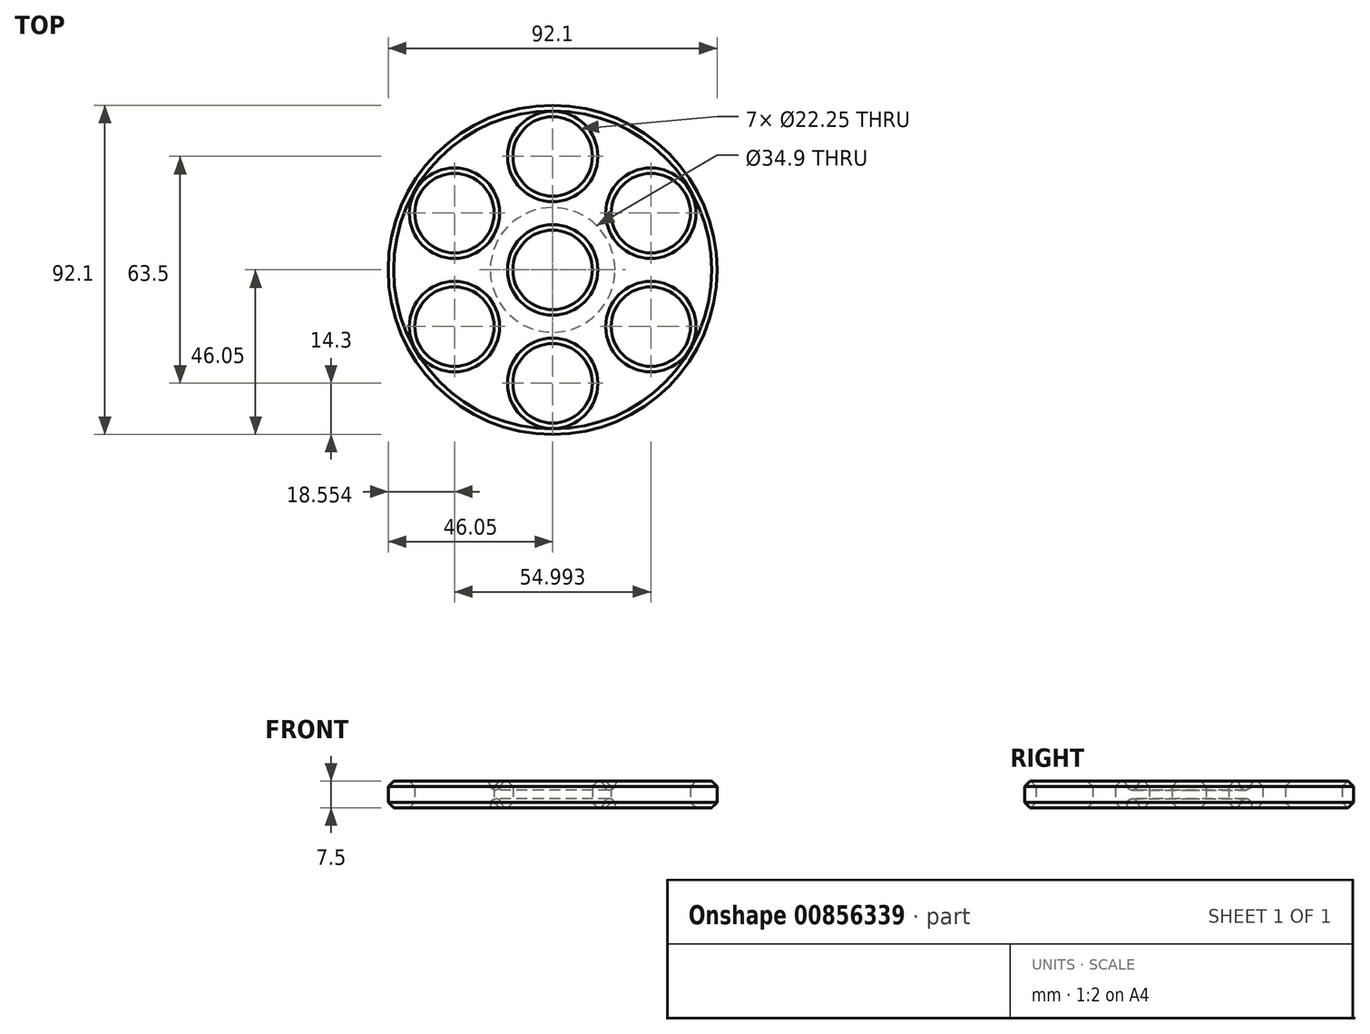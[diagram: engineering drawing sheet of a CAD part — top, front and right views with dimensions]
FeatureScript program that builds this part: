
annotation { "Feature Type Name" : "Feature", "Feature Type Description" : "" }
export const myFeature = defineFeature(function(context is Context, id is Id, definition is map)
    precondition{}
    {
        {
            var Q0;
            Q0=qCreatedBy(makeId("Top.planeOp"),FACE);
            var sketch = newSketch(context, id + "F0", { "sketchPlane" : qUnion([Q0])});
            skCircle(sketch, "E0", {"center": v(0, 0) * mm, "radius": 11.12 * mm});
            skCircle(sketch, "E1", {"center": v(0, 31.75) * mm, "radius": 11.12 * mm});
            skCircle(sketch, "E2", {"center": v(0, -31.75) * mm, "radius": 11.12 * mm});
            skCircle(sketch, "E3", {"center": v(0, 31.75) * mm, "radius": 14.3 * mm});
            skCircle(sketch, "E4", {"center": v(0, 0) * mm, "radius": 14.3 * mm});
            skCircle(sketch, "E5", {"center": v(0, -31.75) * mm, "radius": 14.3 * mm});
            skCircle(sketch, "E6", {"center": v(0, 0) * mm, "radius": 42.88 * mm});
            skCircle(sketch, "E7", {"center": v(0, 0) * mm, "radius": 46.05 * mm});
            skCircle(sketch, "E8.1.0", {"center": v(27.5, 15.87) * mm, "radius": 14.3 * mm});
            skCircle(sketch, "E8.1.1", {"center": v(27.5, 15.87) * mm, "radius": 11.12 * mm});
            skCircle(sketch, "E8.1.2", {"center": v(-27.5, -15.87) * mm, "radius": 11.12 * mm});
            skCircle(sketch, "E8.1.3", {"center": v(-27.5, -15.87) * mm, "radius": 14.3 * mm});
            skCircle(sketch, "E8.2.0", {"center": v(-27.5, 15.88) * mm, "radius": 14.3 * mm});
            skCircle(sketch, "E8.2.1", {"center": v(-27.5, 15.88) * mm, "radius": 11.12 * mm});
            skCircle(sketch, "E8.2.2", {"center": v(27.5, -15.88) * mm, "radius": 11.12 * mm});
            skCircle(sketch, "E8.2.3", {"center": v(27.5, -15.88) * mm, "radius": 14.3 * mm});
            skCircle(sketch, "E9", {"center": v(0, 0) * mm, "radius": 20.62 * mm});
            skCircle(sketch, "E10", {"center": v(0, 0) * mm, "radius": 17.45 * mm});
            skSolve(sketch);
        }
        {
            var Q0;
            Q0 = qSketchRegion(id + "F0", true);
            var Q1;
            {var subQ0=sQuery(id+"F0.wireOp",EDGE,"E6");var subQ1=sQuery(id+"F0.wireOp",EDGE,"E1");var subQ2=makeQuery(id+"F0.imprint","INTERSECT",VERTEX,{"derivedFrom":[subQ1,subQ0]});Q1=makeQuery(id+"F0.imprint","IMPRINT",FACE,{"disambiguationData":[TD([[makeQuery(id+"F0.imprint","IMPRINT",EDGE,{"disambiguationData":[TD([[subQ2,1.0]])],"derivedFrom":subQ1}),-1.0]])]});}
            var Q2;
            {var subQ0=sQuery(id+"F0.wireOp",EDGE,"E6");var subQ1=sQuery(id+"F0.wireOp",EDGE,"E1");var subQ2=makeQuery(id+"F0.imprint","INTERSECT",VERTEX,{"derivedFrom":[subQ1,subQ0]});Q2=makeQuery(id+"F0.imprint","IMPRINT",FACE,{"disambiguationData":[TD([[makeQuery(id+"F0.imprint","IMPRINT",EDGE,{"disambiguationData":[TD([[subQ2,-1.0]])],"derivedFrom":subQ1}),-1.0]])]});}
            var Q3;
            {var subQ0=sQuery(id+"F0.wireOp",EDGE,"E9");var subQ1=sQuery(id+"F0.wireOp",EDGE,"E3");var subQ2=makeQuery(id+"F0.imprint","INTERSECT",VERTEX,{"disambiguationData":[OD(0.0)],"derivedFrom":[subQ1,subQ0]});Q3=makeQuery(id+"F0.imprint","IMPRINT",FACE,{"disambiguationData":[TD([[makeQuery(id+"F0.imprint","IMPRINT",EDGE,{"disambiguationData":[TD([[subQ2,-1.0]])],"derivedFrom":subQ1}),1.0]])]});}
            var Q4;
            {var subQ0=sQuery(id+"F0.wireOp",EDGE,"E8.1.0");var subQ1=makeQuery(id+"F0.imprint","INTERSECT",VERTEX,{"derivedFrom":[subQ0,sQuery(id+"F0.wireOp",EDGE,"E10")]});Q4=makeQuery(id+"F0.imprint","IMPRINT",FACE,{"disambiguationData":[TD([[makeQuery(id+"F0.imprint","IMPRINT",EDGE,{"disambiguationData":[TD([[subQ1,1.0]])],"derivedFrom":subQ0}),1.0]])]});}
            var Q5;
            {var subQ0=sQuery(id+"F0.wireOp",EDGE,"E10");var subQ1=sQuery(id+"F0.wireOp",EDGE,"E3");var subQ2=makeQuery(id+"F0.imprint","INTERSECT",VERTEX,{"derivedFrom":[subQ1,subQ0]});Q5=makeQuery(id+"F0.imprint","IMPRINT",FACE,{"disambiguationData":[TD([[makeQuery(id+"F0.imprint","IMPRINT",EDGE,{"disambiguationData":[TD([[subQ2,-1.0]])],"derivedFrom":subQ1}),-1.0]])]});}
            var Q6;
            {var subQ0=sQuery(id+"F0.wireOp",EDGE,"E10");var subQ1=sQuery(id+"F0.wireOp",EDGE,"E8.1.0");var subQ2=makeQuery(id+"F0.imprint","INTERSECT",VERTEX,{"derivedFrom":[subQ1,subQ0]});Q6=makeQuery(id+"F0.imprint","IMPRINT",FACE,{"disambiguationData":[TD([[makeQuery(id+"F0.imprint","IMPRINT",EDGE,{"disambiguationData":[TD([[subQ2,-1.0]])],"derivedFrom":subQ1}),-1.0]])]});}
            var Q7;
            {var subQ0=sQuery(id+"F0.wireOp",EDGE,"E9");var subQ1=sQuery(id+"F0.wireOp",EDGE,"E8.2.3");var subQ2=makeQuery(id+"F0.imprint","INTERSECT",VERTEX,{"disambiguationData":[OD(0.0)],"derivedFrom":[subQ1,subQ0]});Q7=makeQuery(id+"F0.imprint","IMPRINT",FACE,{"disambiguationData":[TD([[makeQuery(id+"F0.imprint","IMPRINT",EDGE,{"disambiguationData":[TD([[subQ2,-1.0]])],"derivedFrom":subQ1}),1.0]])]});}
            var Q8;
            {var subQ0=sQuery(id+"F0.wireOp",EDGE,"E10");var subQ1=sQuery(id+"F0.wireOp",EDGE,"E5");var subQ2=makeQuery(id+"F0.imprint","INTERSECT",VERTEX,{"derivedFrom":[subQ1,subQ0]});Q8=makeQuery(id+"F0.imprint","IMPRINT",FACE,{"disambiguationData":[TD([[makeQuery(id+"F0.imprint","IMPRINT",EDGE,{"disambiguationData":[TD([[subQ2,1.0]])],"derivedFrom":subQ1}),-1.0]])]});}
            var Q9;
            {var subQ0=sQuery(id+"F0.wireOp",EDGE,"E5");var subQ1=makeQuery(id+"F0.imprint","INTERSECT",VERTEX,{"derivedFrom":[subQ0,sQuery(id+"F0.wireOp",EDGE,"E10")]});Q9=makeQuery(id+"F0.imprint","IMPRINT",FACE,{"disambiguationData":[TD([[makeQuery(id+"F0.imprint","IMPRINT",EDGE,{"disambiguationData":[TD([[subQ1,1.0]])],"derivedFrom":subQ0}),1.0]])]});}
            var Q10;
            {var subQ0=sQuery(id+"F0.wireOp",EDGE,"E10");var subQ1=sQuery(id+"F0.wireOp",EDGE,"E5");var subQ2=makeQuery(id+"F0.imprint","INTERSECT",VERTEX,{"derivedFrom":[subQ1,subQ0]});Q10=makeQuery(id+"F0.imprint","IMPRINT",FACE,{"disambiguationData":[TD([[makeQuery(id+"F0.imprint","IMPRINT",EDGE,{"disambiguationData":[TD([[subQ2,-1.0]])],"derivedFrom":subQ1}),-1.0]])]});}
            var Q11;
            {var subQ0=sQuery(id+"F0.wireOp",EDGE,"E9");var subQ1=sQuery(id+"F0.wireOp",EDGE,"E8.1.3");var subQ2=makeQuery(id+"F0.imprint","INTERSECT",VERTEX,{"disambiguationData":[OD(0.0)],"derivedFrom":[subQ1,subQ0]});Q11=makeQuery(id+"F0.imprint","IMPRINT",FACE,{"disambiguationData":[TD([[makeQuery(id+"F0.imprint","IMPRINT",EDGE,{"disambiguationData":[TD([[subQ2,-1.0]])],"derivedFrom":subQ1}),1.0]])]});}
            var Q12;
            {var subQ0=sQuery(id+"F0.wireOp",EDGE,"E10");var subQ1=sQuery(id+"F0.wireOp",EDGE,"E8.1.3");var subQ2=makeQuery(id+"F0.imprint","INTERSECT",VERTEX,{"derivedFrom":[subQ1,subQ0]});Q12=makeQuery(id+"F0.imprint","IMPRINT",FACE,{"disambiguationData":[TD([[makeQuery(id+"F0.imprint","IMPRINT",EDGE,{"disambiguationData":[TD([[subQ2,-1.0]])],"derivedFrom":subQ1}),-1.0]])]});}
            var Q13;
            {var subQ0=sQuery(id+"F0.wireOp",EDGE,"E8.2.0");var subQ1=makeQuery(id+"F0.imprint","INTERSECT",VERTEX,{"derivedFrom":[subQ0,sQuery(id+"F0.wireOp",EDGE,"E10")]});Q13=makeQuery(id+"F0.imprint","IMPRINT",FACE,{"disambiguationData":[TD([[makeQuery(id+"F0.imprint","IMPRINT",EDGE,{"disambiguationData":[TD([[subQ1,1.0]])],"derivedFrom":subQ0}),1.0]])]});}
            var Q14;
            {var subQ0=sQuery(id+"F0.wireOp",EDGE,"E9");var subQ1=sQuery(id+"F0.wireOp",EDGE,"E3");var subQ2=makeQuery(id+"F0.imprint","INTERSECT",VERTEX,{"disambiguationData":[OD(0.0)],"derivedFrom":[subQ1,subQ0]});Q14=makeQuery(id+"F0.imprint","IMPRINT",FACE,{"disambiguationData":[TD([[makeQuery(id+"F0.imprint","IMPRINT",EDGE,{"disambiguationData":[TD([[subQ2,-1.0]])],"derivedFrom":subQ1}),-1.0]])]});}
            var Q15;
            {var subQ0=sQuery(id+"F0.wireOp",EDGE,"E8.2.0");var subQ1=sQuery(id+"F0.wireOp",EDGE,"E6");var subQ2=makeQuery(id+"F0.imprint","INTERSECT",VERTEX,{"disambiguationData":[OD(0.0)],"derivedFrom":[subQ1,subQ0]});Q15=makeQuery(id+"F0.imprint","IMPRINT",FACE,{"disambiguationData":[TD([[makeQuery(id+"F0.imprint","IMPRINT",EDGE,{"disambiguationData":[TD([[subQ2,-1.0]])],"derivedFrom":subQ1}),1.0]])]});}
            var Q16;
            {var subQ0=sQuery(id+"F0.wireOp",EDGE,"E8.2.1");var subQ1=sQuery(id+"F0.wireOp",EDGE,"E6");var subQ2=makeQuery(id+"F0.imprint","INTERSECT",VERTEX,{"derivedFrom":[subQ1,subQ0]});Q16=makeQuery(id+"F0.imprint","IMPRINT",FACE,{"disambiguationData":[TD([[makeQuery(id+"F0.imprint","IMPRINT",EDGE,{"disambiguationData":[TD([[subQ2,-1.0]])],"derivedFrom":subQ1}),1.0]])]});}
            var Q17;
            {var subQ0=sQuery(id+"F0.wireOp",EDGE,"E8.2.0");var subQ1=sQuery(id+"F0.wireOp",EDGE,"E6");var subQ2=makeQuery(id+"F0.imprint","INTERSECT",VERTEX,{"disambiguationData":[OD(1.0)],"derivedFrom":[subQ1,subQ0]});Q17=makeQuery(id+"F0.imprint","IMPRINT",FACE,{"disambiguationData":[TD([[makeQuery(id+"F0.imprint","IMPRINT",EDGE,{"disambiguationData":[TD([[subQ2,-1.0]])],"derivedFrom":subQ1}),1.0]])]});}
            var Q18;
            {var subQ0=sQuery(id+"F0.wireOp",EDGE,"E6");var subQ1=sQuery(id+"F0.wireOp",EDGE,"E3");var subQ2=makeQuery(id+"F0.imprint","INTERSECT",VERTEX,{"disambiguationData":[OD(1.0)],"derivedFrom":[subQ1,subQ0]});Q18=makeQuery(id+"F0.imprint","IMPRINT",FACE,{"disambiguationData":[TD([[makeQuery(id+"F0.imprint","IMPRINT",EDGE,{"disambiguationData":[TD([[subQ2,-1.0]])],"derivedFrom":subQ1}),-1.0]])]});}
            var Q19;
            {var subQ0=sQuery(id+"F0.wireOp",EDGE,"E6");var subQ1=sQuery(id+"F0.wireOp",EDGE,"E3");var subQ2=makeQuery(id+"F0.imprint","INTERSECT",VERTEX,{"disambiguationData":[OD(0.0)],"derivedFrom":[subQ1,subQ0]});Q19=makeQuery(id+"F0.imprint","IMPRINT",FACE,{"disambiguationData":[TD([[makeQuery(id+"F0.imprint","IMPRINT",EDGE,{"disambiguationData":[TD([[subQ2,1.0]])],"derivedFrom":subQ1}),-1.0]])]});}
            var Q20;
            {var subQ0=sQuery(id+"F0.wireOp",EDGE,"E8.1.1");var subQ1=sQuery(id+"F0.wireOp",EDGE,"E6");var subQ2=makeQuery(id+"F0.imprint","INTERSECT",VERTEX,{"derivedFrom":[subQ1,subQ0]});Q20=makeQuery(id+"F0.imprint","IMPRINT",FACE,{"disambiguationData":[TD([[makeQuery(id+"F0.imprint","IMPRINT",EDGE,{"disambiguationData":[TD([[subQ2,-1.0]])],"derivedFrom":subQ1}),1.0]])]});}
            var Q21;
            {var subQ0=sQuery(id+"F0.wireOp",EDGE,"E8.1.1");var subQ1=sQuery(id+"F0.wireOp",EDGE,"E6");var subQ2=makeQuery(id+"F0.imprint","INTERSECT",VERTEX,{"derivedFrom":[subQ1,subQ0]});Q21=makeQuery(id+"F0.imprint","IMPRINT",FACE,{"disambiguationData":[TD([[makeQuery(id+"F0.imprint","IMPRINT",EDGE,{"disambiguationData":[TD([[subQ2,1.0]])],"derivedFrom":subQ1}),1.0]])]});}
            var Q22;
            {var subQ0=sQuery(id+"F0.wireOp",EDGE,"E8.1.0");var subQ1=sQuery(id+"F0.wireOp",EDGE,"E6");var subQ2=makeQuery(id+"F0.imprint","INTERSECT",VERTEX,{"disambiguationData":[OD(0.0)],"derivedFrom":[subQ1,subQ0]});Q22=makeQuery(id+"F0.imprint","IMPRINT",FACE,{"disambiguationData":[TD([[makeQuery(id+"F0.imprint","IMPRINT",EDGE,{"disambiguationData":[TD([[subQ2,1.0]])],"derivedFrom":subQ1}),1.0]])]});}
            var Q23;
            {var subQ0=sQuery(id+"F0.wireOp",EDGE,"E8.2.2");var subQ1=sQuery(id+"F0.wireOp",EDGE,"E6");var subQ2=makeQuery(id+"F0.imprint","INTERSECT",VERTEX,{"derivedFrom":[subQ1,subQ0]});Q23=makeQuery(id+"F0.imprint","IMPRINT",FACE,{"disambiguationData":[TD([[makeQuery(id+"F0.imprint","IMPRINT",EDGE,{"disambiguationData":[TD([[subQ2,-1.0]])],"derivedFrom":subQ1}),1.0]])]});}
            var Q24;
            {var subQ0=sQuery(id+"F0.wireOp",EDGE,"E8.2.3");var subQ1=sQuery(id+"F0.wireOp",EDGE,"E6");var subQ2=makeQuery(id+"F0.imprint","INTERSECT",VERTEX,{"disambiguationData":[OD(0.0)],"derivedFrom":[subQ1,subQ0]});Q24=makeQuery(id+"F0.imprint","IMPRINT",FACE,{"disambiguationData":[TD([[makeQuery(id+"F0.imprint","IMPRINT",EDGE,{"disambiguationData":[TD([[subQ2,-1.0]])],"derivedFrom":subQ1}),1.0]])]});}
            var Q25;
            {var subQ0=sQuery(id+"F0.wireOp",EDGE,"E6");var subQ1=sQuery(id+"F0.wireOp",EDGE,"E2");var subQ2=makeQuery(id+"F0.imprint","INTERSECT",VERTEX,{"derivedFrom":[subQ1,subQ0]});Q25=makeQuery(id+"F0.imprint","IMPRINT",FACE,{"disambiguationData":[TD([[makeQuery(id+"F0.imprint","IMPRINT",EDGE,{"disambiguationData":[TD([[subQ2,1.0]])],"derivedFrom":subQ1}),-1.0]])]});}
            var Q26;
            {var subQ0=sQuery(id+"F0.wireOp",EDGE,"E9");var subQ1=sQuery(id+"F0.wireOp",EDGE,"E5");var subQ2=makeQuery(id+"F0.imprint","INTERSECT",VERTEX,{"disambiguationData":[OD(1.0)],"derivedFrom":[subQ1,subQ0]});Q26=makeQuery(id+"F0.imprint","IMPRINT",FACE,{"disambiguationData":[TD([[makeQuery(id+"F0.imprint","IMPRINT",EDGE,{"disambiguationData":[TD([[subQ2,-1.0]])],"derivedFrom":subQ1}),-1.0]])]});}
            var Q27;
            {var subQ0=sQuery(id+"F0.wireOp",EDGE,"E9");var subQ1=sQuery(id+"F0.wireOp",EDGE,"E5");var subQ2=makeQuery(id+"F0.imprint","INTERSECT",VERTEX,{"disambiguationData":[OD(0.0)],"derivedFrom":[subQ1,subQ0]});Q27=makeQuery(id+"F0.imprint","IMPRINT",FACE,{"disambiguationData":[TD([[makeQuery(id+"F0.imprint","IMPRINT",EDGE,{"disambiguationData":[TD([[subQ2,1.0]])],"derivedFrom":subQ1}),-1.0]])]});}
            var Q28;
            {var subQ0=sQuery(id+"F0.wireOp",EDGE,"E6");var subQ1=sQuery(id+"F0.wireOp",EDGE,"E2");var subQ2=makeQuery(id+"F0.imprint","INTERSECT",VERTEX,{"derivedFrom":[subQ1,subQ0]});Q28=makeQuery(id+"F0.imprint","IMPRINT",FACE,{"disambiguationData":[TD([[makeQuery(id+"F0.imprint","IMPRINT",EDGE,{"disambiguationData":[TD([[subQ2,-1.0]])],"derivedFrom":subQ1}),-1.0]])]});}
            var Q29;
            {var subQ0=sQuery(id+"F0.wireOp",EDGE,"E8.1.2");var subQ1=sQuery(id+"F0.wireOp",EDGE,"E6");var subQ2=makeQuery(id+"F0.imprint","INTERSECT",VERTEX,{"derivedFrom":[subQ1,subQ0]});Q29=makeQuery(id+"F0.imprint","IMPRINT",FACE,{"disambiguationData":[TD([[makeQuery(id+"F0.imprint","IMPRINT",EDGE,{"disambiguationData":[TD([[subQ2,-1.0]])],"derivedFrom":subQ1}),1.0]])]});}
            var Q30;
            {var subQ0=sQuery(id+"F0.wireOp",EDGE,"E8.1.3");var subQ1=sQuery(id+"F0.wireOp",EDGE,"E6");var subQ2=makeQuery(id+"F0.imprint","INTERSECT",VERTEX,{"disambiguationData":[OD(0.0)],"derivedFrom":[subQ1,subQ0]});Q30=makeQuery(id+"F0.imprint","IMPRINT",FACE,{"disambiguationData":[TD([[makeQuery(id+"F0.imprint","IMPRINT",EDGE,{"disambiguationData":[TD([[subQ2,-1.0]])],"derivedFrom":subQ1}),1.0]])]});}
            var Q31;
            Q31=makeQuery(id+"F0.imprint","IMPRINT",FACE,{"disambiguationData":[TD([[makeQuery(id+"F0.imprint","IMPRINT",EDGE,{"derivedFrom":sQuery(id+"F0.wireOp",EDGE,"E0")}),-1.0]])]});
            var Q32;
            Q32=makeQuery(id+"F0.imprint","IMPRINT",FACE,{"disambiguationData":[TD([[makeQuery(id+"F0.imprint","IMPRINT",EDGE,{"derivedFrom":sQuery(id+"F0.wireOp",EDGE,"E4")}),-1.0]])]});
            extrude(context, id + "F1", {"entities" : qUnion([Q0, Q1, Q2, Q3, Q4, Q5, Q6, Q7, Q8, Q9, Q10, Q11, Q12, Q13, Q14, Q15, Q16, Q17, Q18, Q19, Q20, Q21, Q22, Q23, Q24, Q25, Q26, Q27, Q28, Q29, Q30, Q31, Q32]), "depth" : 7.5 * mm, "offsetDistance" : 25 * mm});
        }
        {
            var Q0;
            Q0=makeQuery(id+"F0.imprint","IMPRINT",FACE,{"disambiguationData":[TD([[makeQuery(id+"F0.imprint","IMPRINT",EDGE,{"derivedFrom":sQuery(id+"F0.wireOp",EDGE,"E4")}),-1.0]])]});
            extrude(context, id + "F2", {"entities" : qUnion([Q0]), "operationType" : NewBodyOperationType.REMOVE, "depth" : 7.5 / 3 * mm, "offsetDistance" : 25 * mm});
        }
        {
            var Q0;
            Q0=makeQuery(id+"F0.imprint","IMPRINT",FACE,{"disambiguationData":[TD([[makeQuery(id+"F0.imprint","IMPRINT",EDGE,{"derivedFrom":sQuery(id+"F0.wireOp",EDGE,"E4")}),-1.0]])]});
            extrude(context, id + "F3", {"entities" : qUnion([Q0]), "operationType" : NewBodyOperationType.REMOVE, "depth" : 25 * mm, "offsetDistance" : 25 * mm, "hasSecondDirection" : true, "secondDirectionOppositeDirection" : false, "secondDirectionDepth" : (7.5 / 3) * 2 * mm});
        }
        {
            var Q0;
            Q0=makeQuery(id+"F3.boolean.opBoolean","COPY",EDGE,{"derivedFrom":makeQuery(id+"F3.opExtrude","CAP_EDGE",EDGE,{"disambiguationData":[OSD([sQuery(id+"F0.wireOp",EDGE,"E10")])],"isStart":true})});
            var Q1;
            Q1=makeQuery(id+"F3.boolean.opBoolean","COPY",EDGE,{"derivedFrom":makeQuery(id+"F3.opExtrude","CAP_EDGE",EDGE,{"disambiguationData":[OSD([sQuery(id+"F0.wireOp",EDGE,"E4")])],"isStart":true})});
            var Q2;
            Q2=makeQuery(id+"F2.boolean.opBoolean","COPY",EDGE,{"derivedFrom":makeQuery(id+"F2.opExtrude","CAP_EDGE",EDGE,{"disambiguationData":[OSD([sQuery(id+"F0.wireOp",EDGE,"E4")])],"isStart":false})});
            var Q3;
            Q3=makeQuery(id+"F2.boolean.opBoolean","COPY",FACE,{"derivedFrom":makeQuery(id+"F2.opExtrude","CAP_FACE",FACE,{"disambiguationData":[OSD([sQuery(id+"F0.wireOp",EDGE,"E4"),sQuery(id+"F0.wireOp",EDGE,"E10")])],"isStart":false})});
            fillet(context, id + "F4", {"entities" : qUnion([Q0, Q1, Q2, Q3]), "radius" : 1.52 * mm, "tangentPropagation" : true, "allowEdgeOverflow" : false});
        }
        {
            var Q0;
            Q0=makeQuery(id+"F3.boolean.opBoolean","INTERSECT",EDGE,{"derivedFrom":[makeQuery(id+"F1.opExtrude","CAP_FACE",FACE,{"disambiguationData":[OSD([sQuery(id+"F0.wireOp",EDGE,"E0"),sQuery(id+"F0.wireOp",EDGE,"E1"),sQuery(id+"F0.wireOp",EDGE,"E2"),sQuery(id+"F0.wireOp",EDGE,"E7"),sQuery(id+"F0.wireOp",EDGE,"E8.1.1"),sQuery(id+"F0.wireOp",EDGE,"E8.1.2"),sQuery(id+"F0.wireOp",EDGE,"E8.2.1"),sQuery(id+"F0.wireOp",EDGE,"E8.2.2")])],"isStart":false}),makeQuery(id+"F3.opExtrude","SWEPT_FACE",FACE,{"disambiguationData":[OSD([sQuery(id+"F0.wireOp",EDGE,"E10")])]})]});
            var Q1;
            Q1=makeQuery(id+"F3.boolean.opBoolean","INTERSECT",EDGE,{"derivedFrom":[makeQuery(id+"F1.opExtrude","CAP_FACE",FACE,{"disambiguationData":[OSD([sQuery(id+"F0.wireOp",EDGE,"E0"),sQuery(id+"F0.wireOp",EDGE,"E1"),sQuery(id+"F0.wireOp",EDGE,"E2"),sQuery(id+"F0.wireOp",EDGE,"E7"),sQuery(id+"F0.wireOp",EDGE,"E8.1.1"),sQuery(id+"F0.wireOp",EDGE,"E8.1.2"),sQuery(id+"F0.wireOp",EDGE,"E8.2.1"),sQuery(id+"F0.wireOp",EDGE,"E8.2.2")])],"isStart":false}),makeQuery(id+"F3.opExtrude","SWEPT_FACE",FACE,{"disambiguationData":[OSD([sQuery(id+"F0.wireOp",EDGE,"E4")])]})]});
            var Q2;
            Q2=makeQuery(id+"F2.boolean.opBoolean","COPY",EDGE,{"derivedFrom":makeQuery(id+"F2.opExtrude","CAP_EDGE",EDGE,{"disambiguationData":[OSD([sQuery(id+"F0.wireOp",EDGE,"E4")])],"isStart":true})});
            var Q3;
            Q3=makeQuery(id+"F2.boolean.opBoolean","COPY",EDGE,{"derivedFrom":makeQuery(id+"F2.opExtrude","CAP_EDGE",EDGE,{"disambiguationData":[OSD([sQuery(id+"F0.wireOp",EDGE,"E10")])],"isStart":true})});
            fillet(context, id + "F5", {"entities" : qUnion([Q0, Q1, Q2, Q3]), "radius" : 1.59 * mm, "tangentPropagation" : true, "allowEdgeOverflow" : false});
        }
        {
            var Q0;
            Q0=makeQuery(id+"F1.opExtrude","SWEPT_FACE",FACE,{"disambiguationData":[OSD([sQuery(id+"F0.wireOp",EDGE,"E0")])]});
            var Q1;
            Q1=makeQuery(id+"F1.opExtrude","SWEPT_FACE",FACE,{"disambiguationData":[OSD([sQuery(id+"F0.wireOp",EDGE,"E7")])]});
            var Q2;
            Q2=makeQuery(id+"F1.opExtrude","SWEPT_FACE",FACE,{"disambiguationData":[OSD([sQuery(id+"F0.wireOp",EDGE,"E2")])]});
            var Q3;
            Q3=makeQuery(id+"F1.opExtrude","SWEPT_FACE",FACE,{"disambiguationData":[OSD([sQuery(id+"F0.wireOp",EDGE,"E8.1.2")])]});
            var Q4;
            Q4=makeQuery(id+"F1.opExtrude","SWEPT_FACE",FACE,{"disambiguationData":[OSD([sQuery(id+"F0.wireOp",EDGE,"E8.2.1")])]});
            var Q5;
            Q5=makeQuery(id+"F1.opExtrude","SWEPT_FACE",FACE,{"disambiguationData":[OSD([sQuery(id+"F0.wireOp",EDGE,"E1")])]});
            var Q6;
            Q6=makeQuery(id+"F1.opExtrude","SWEPT_FACE",FACE,{"disambiguationData":[OSD([sQuery(id+"F0.wireOp",EDGE,"E8.1.1")])]});
            var Q7;
            Q7=makeQuery(id+"F1.opExtrude","SWEPT_FACE",FACE,{"disambiguationData":[OSD([sQuery(id+"F0.wireOp",EDGE,"E8.2.2")])]});
            chamfer(context, id + "F6", {"entities" : qUnion([Q0, Q1, Q2, Q3, Q4, Q5, Q6, Q7]), "width" : 1.52 * mm, "tangentPropagation" : true});
        }
    });
